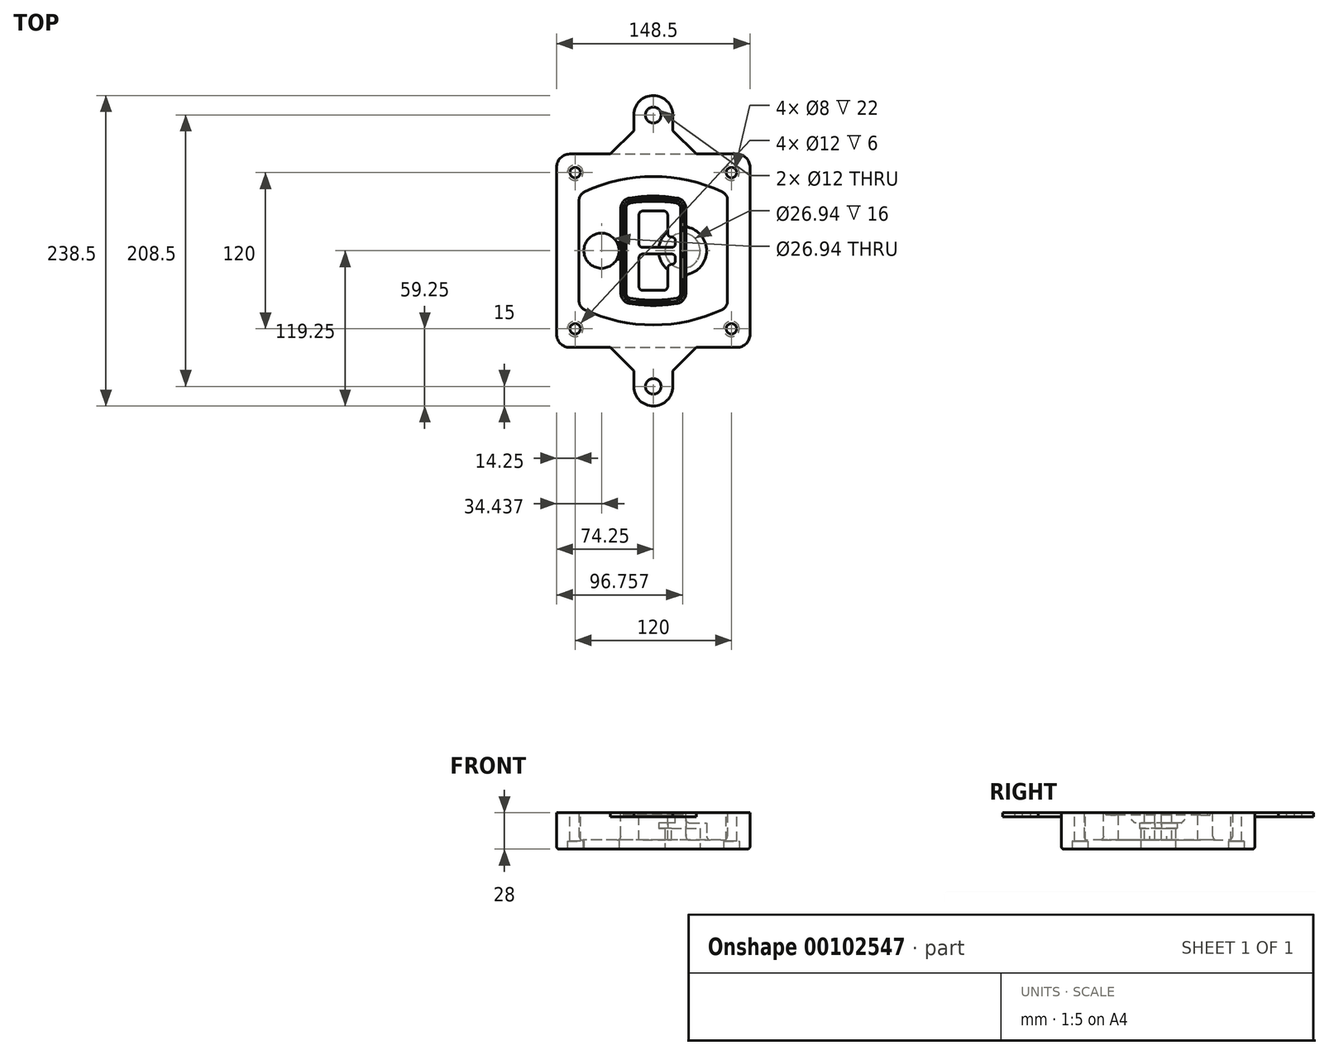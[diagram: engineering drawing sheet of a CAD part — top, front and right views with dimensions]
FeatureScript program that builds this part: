
annotation { "Feature Type Name" : "Feature", "Feature Type Description" : "" }
export const myFeature = defineFeature(function(context is Context, id is Id, definition is map)
    precondition{}
    {
        {
            var Q0;
            Q0=qCreatedBy(makeId("Top.planeOp"),FACE);
            var sketch = newSketch(context, id + "F0", { "sketchPlane" : qUnion([Q0])});
            skPoint(sketch, "E0.rect.middle", {"position": v(0, 0) * mm});
            skLineSegment(sketch, "E1.bottom", {"start": v(-64.25, -74.25) * mm, "end": v(64.25, -74.25) * mm});
            skLineSegment(sketch, "E1.top", {"start": v(-64.25, 74.25) * mm, "end": v(64.25, 74.25) * mm});
            skLineSegment(sketch, "E1.left", {"start": v(-74.25, -64.25) * mm, "end": v(-74.25, 64.25) * mm});
            skLineSegment(sketch, "E1.right", {"start": v(74.25, -64.25) * mm, "end": v(74.25, 64.25) * mm});
            skLineSegment(sketch, "E2", {"start": v(-74.25, 74.25) * mm, "end": v(74.25, -74.25) * mm, "construction": true});
            skLineSegment(sketch, "E3", {"start": v(74.25, 74.25) * mm, "end": v(-74.25, -74.25) * mm, "construction": true});
            skCircle(sketch, "E4", {"center": v(-60, 60) * mm, "radius": 4 * mm});
            skCircle(sketch, "E5", {"center": v(60, 60) * mm, "radius": 4 * mm});
            skCircle(sketch, "E6", {"center": v(60, -60) * mm, "radius": 4 * mm});
            skCircle(sketch, "E7", {"center": v(-60, -60) * mm, "radius": 4 * mm});
            skLineSegment(sketch, "E8", {"start": v(-60, 60) * mm, "end": v(60, 60) * mm, "construction": true});
            skLineSegment(sketch, "E9", {"start": v(60, 60) * mm, "end": v(60, -60) * mm, "construction": true});
            skLineSegment(sketch, "E10", {"start": v(60, -60) * mm, "end": v(-60, -60) * mm, "construction": true});
            skLineSegment(sketch, "E11", {"start": v(-60, -60) * mm, "end": v(-60, 60) * mm, "construction": true});
            skLineSegment(sketch, "E12", {"start": v(-60, 38.83) * mm, "end": v(-60, -38.83) * mm});
            skLineSegment(sketch, "E13", {"start": v(60, 38.83) * mm, "end": v(60, -38.83) * mm});
            skArc(sketch, "E14", {"start": v(54.26, 47.88) * mm, "mid": v(0, 60) * mm, "end": v(-54.26, 47.88) * mm});
            skArc(sketch, "E15", {"start": v(-54.26, -47.88) * mm, "mid": v(0, -60) * mm, "end": v(54.26, -47.88) * mm});
            skLineSegment(sketch, "E16", {"start": v(-60, 0) * mm, "end": v(60, 0) * mm, "construction": true});
            skPoint(sketch, "E17.visualSharp", {"position": v(-60, -45) * mm});
            skArc(sketch, "E17.filletArc", {"start": v(-60, -38.83) * mm, "mid": v(-58.44, -44.2) * mm, "end": v(-54.26, -47.88) * mm});
            skPoint(sketch, "E18.visualSharp", {"position": v(-60, 45) * mm});
            skArc(sketch, "E18.filletArc", {"start": v(-54.26, 47.88) * mm, "mid": v(-58.44, 44.2) * mm, "end": v(-60, 38.83) * mm});
            skPoint(sketch, "E19.visualSharp", {"position": v(60, 45) * mm});
            skArc(sketch, "E19.filletArc", {"start": v(60, 38.83) * mm, "mid": v(58.44, 44.2) * mm, "end": v(54.26, 47.88) * mm});
            skPoint(sketch, "E20.visualSharp", {"position": v(60, -45) * mm});
            skArc(sketch, "E20.filletArc", {"start": v(54.26, -47.88) * mm, "mid": v(58.44, -44.2) * mm, "end": v(60, -38.83) * mm});
            skPoint(sketch, "E21.visualSharp", {"position": v(-74.25, 74.25) * mm});
            skArc(sketch, "E21.filletArc", {"start": v(-64.25, 74.25) * mm, "mid": v(-71.32, 71.32) * mm, "end": v(-74.25, 64.25) * mm});
            skPoint(sketch, "E22.visualSharp", {"position": v(74.25, 74.25) * mm});
            skArc(sketch, "E22.filletArc", {"start": v(74.25, 64.25) * mm, "mid": v(71.32, 71.32) * mm, "end": v(64.25, 74.25) * mm});
            skPoint(sketch, "E23.visualSharp", {"position": v(74.25, -74.25) * mm});
            skArc(sketch, "E23.filletArc", {"start": v(64.25, -74.25) * mm, "mid": v(71.32, -71.32) * mm, "end": v(74.25, -64.25) * mm});
            skPoint(sketch, "E24.visualSharp", {"position": v(-74.25, -74.25) * mm});
            skArc(sketch, "E24.filletArc", {"start": v(-74.25, -64.25) * mm, "mid": v(-71.32, -71.32) * mm, "end": v(-64.25, -74.25) * mm});
            skArc(sketch, "E25.0", {"start": v(57, 38.83) * mm, "mid": v(55.9, 42.58) * mm, "end": v(52.98, 45.17) * mm});
            skLineSegment(sketch, "E25.1", {"start": v(57, 38.83) * mm, "end": v(57, -38.83) * mm});
            skArc(sketch, "E25.2", {"start": v(52.98, -45.17) * mm, "mid": v(55.9, -42.58) * mm, "end": v(57, -38.83) * mm});
            skArc(sketch, "E25.3", {"start": v(-52.98, -45.17) * mm, "mid": v(0, -57) * mm, "end": v(52.98, -45.17) * mm});
            skArc(sketch, "E25.4", {"start": v(-57, -38.83) * mm, "mid": v(-55.9, -42.58) * mm, "end": v(-52.98, -45.17) * mm});
            skArc(sketch, "E25.5", {"start": v(52.98, 45.17) * mm, "mid": v(0, 57) * mm, "end": v(-52.98, 45.17) * mm});
            skLineSegment(sketch, "E25.6", {"start": v(-57, 38.83) * mm, "end": v(-57, -38.83) * mm});
            skArc(sketch, "E25.7", {"start": v(-52.98, 45.17) * mm, "mid": v(-55.9, 42.58) * mm, "end": v(-57, 38.83) * mm});
            skArc(sketch, "E26.0", {"start": v(-55.96, 51.5) * mm, "mid": v(-61.82, 46.33) * mm, "end": v(-64, 38.83) * mm});
            skArc(sketch, "E26.1", {"start": v(55.96, 51.5) * mm, "mid": v(0, 64) * mm, "end": v(-55.96, 51.5) * mm});
            skArc(sketch, "E26.2", {"start": v(64, 38.83) * mm, "mid": v(61.82, 46.33) * mm, "end": v(55.96, 51.5) * mm});
            skLineSegment(sketch, "E26.3", {"start": v(64, 38.83) * mm, "end": v(64, -38.83) * mm});
            skArc(sketch, "E26.4", {"start": v(55.96, -51.5) * mm, "mid": v(61.82, -46.33) * mm, "end": v(64, -38.83) * mm});
            skLineSegment(sketch, "E26.5", {"start": v(-64, 38.83) * mm, "end": v(-64, -38.83) * mm});
            skArc(sketch, "E26.6", {"start": v(-55.96, -51.5) * mm, "mid": v(0, -64) * mm, "end": v(55.96, -51.5) * mm});
            skArc(sketch, "E26.7", {"start": v(-64, -38.83) * mm, "mid": v(-61.82, -46.33) * mm, "end": v(-55.96, -51.5) * mm});
            skSolve(sketch);
        }
        {
            var Q0;
            Q0=makeQuery(id+"F0.imprint","IMPRINT",FACE,{"disambiguationData":[TD([[makeQuery(id+"F0.imprint","IMPRINT",EDGE,{"derivedFrom":sQuery(id+"F0.wireOp",EDGE,"E1.bottom")}),1.0]])]});
            var Q1;
            Q1=makeQuery(id+"F0.imprint","IMPRINT",FACE,{"disambiguationData":[TD([[makeQuery(id+"F0.imprint","IMPRINT",EDGE,{"derivedFrom":sQuery(id+"F0.wireOp",EDGE,"E12")}),1.0]])]});
            var Q2;
            Q2=makeQuery(id+"F0.imprint","IMPRINT",FACE,{"disambiguationData":[TD([[makeQuery(id+"F0.imprint","IMPRINT",EDGE,{"derivedFrom":sQuery(id+"F0.wireOp",EDGE,"E25.0")}),1.0]])]});
            var Q3;
            Q3=makeQuery(id+"F0.imprint","IMPRINT",FACE,{"disambiguationData":[TD([[makeQuery(id+"F0.imprint","IMPRINT",EDGE,{"derivedFrom":sQuery(id+"F0.wireOp",EDGE,"E12")}),-1.0]])]});
            extrude(context, id + "F1", {"entities" : qUnion([Q0, Q1, Q2, Q3]), "oppositeDirection" : true, "depth" : 25 * mm});
        }
        {
            var Q0;
            Q0=makeQuery(id+"F0.imprint","IMPRINT",FACE,{"disambiguationData":[TD([[makeQuery(id+"F0.imprint","IMPRINT",EDGE,{"derivedFrom":sQuery(id+"F0.wireOp",EDGE,"E12")}),1.0]])]});
            extrude(context, id + "F2", {"entities" : qUnion([Q0]), "operationType" : NewBodyOperationType.ADD, "depth" : 3 * mm});
        }
        {
            var Q0;
            Q0=makeQuery(id+"F0.imprint","IMPRINT",FACE,{"disambiguationData":[TD([[makeQuery(id+"F0.imprint","IMPRINT",EDGE,{"derivedFrom":sQuery(id+"F0.wireOp",EDGE,"E25.0")}),1.0]])]});
            extrude(context, id + "F3", {"entities" : qUnion([Q0]), "operationType" : NewBodyOperationType.REMOVE, "oppositeDirection" : true, "depth" : 18 * mm});
        }
        {
            var Q0;
            Q0=makeQuery(id+"F2.opExtrude","CAP_FACE",FACE,{"disambiguationData":[OSD([sQuery(id+"F0.wireOp",EDGE,"E12"),sQuery(id+"F0.wireOp",EDGE,"E13"),sQuery(id+"F0.wireOp",EDGE,"E14"),sQuery(id+"F0.wireOp",EDGE,"E15"),sQuery(id+"F0.wireOp",EDGE,"E17.filletArc"),sQuery(id+"F0.wireOp",EDGE,"E18.filletArc"),sQuery(id+"F0.wireOp",EDGE,"E19.filletArc"),sQuery(id+"F0.wireOp",EDGE,"E20.filletArc"),sQuery(id+"F0.wireOp",EDGE,"E25.0"),sQuery(id+"F0.wireOp",EDGE,"E25.1"),sQuery(id+"F0.wireOp",EDGE,"E25.2"),sQuery(id+"F0.wireOp",EDGE,"E25.3"),sQuery(id+"F0.wireOp",EDGE,"E25.4"),sQuery(id+"F0.wireOp",EDGE,"E25.5"),sQuery(id+"F0.wireOp",EDGE,"E25.6"),sQuery(id+"F0.wireOp",EDGE,"E25.7")])],"isStart":false});
            var sketch = newSketch(context, id + "F4", { "sketchPlane" : qUnion([Q0])});
            skArc(sketch, "E27.0", {"start": v(-18.34, -40.45) * mm, "mid": v(0, -42) * mm, "end": v(18.34, -40.45) * mm});
            skArc(sketch, "E28.0", {"start": v(18.34, 40.45) * mm, "mid": v(0, 42) * mm, "end": v(-18.34, 40.45) * mm});
            skLineSegment(sketch, "E29", {"start": v(-25, 32.57) * mm, "end": v(-25, -32.57) * mm});
            skLineSegment(sketch, "E30", {"start": v(25, 32.57) * mm, "end": v(25, -32.57) * mm});
            skLineSegment(sketch, "E31", {"start": v(-25, 39.1) * mm, "end": v(25, 39.1) * mm, "construction": true});
            skLineSegment(sketch, "E32", {"start": v(-25, -39.1) * mm, "end": v(25, -39.1) * mm, "construction": true});
            skPoint(sketch, "E33.visualSharp", {"position": v(-25, 39.1) * mm});
            skArc(sketch, "E33.filletArc", {"start": v(-18.34, 40.45) * mm, "mid": v(-23.11, 37.73) * mm, "end": v(-25, 32.57) * mm});
            skPoint(sketch, "E34.visualSharp", {"position": v(25, 39.1) * mm});
            skArc(sketch, "E34.filletArc", {"start": v(25, 32.57) * mm, "mid": v(23.11, 37.73) * mm, "end": v(18.34, 40.45) * mm});
            skPoint(sketch, "E35.visualSharp", {"position": v(25, -39.1) * mm});
            skArc(sketch, "E35.filletArc", {"start": v(18.34, -40.45) * mm, "mid": v(23.11, -37.73) * mm, "end": v(25, -32.57) * mm});
            skPoint(sketch, "E36.visualSharp", {"position": v(-25, -39.1) * mm});
            skArc(sketch, "E36.filletArc", {"start": v(-25, -32.57) * mm, "mid": v(-23.11, -37.73) * mm, "end": v(-18.34, -40.45) * mm});
            skArc(sketch, "E37.0", {"start": v(52.98, 45.17) * mm, "mid": v(0, 57) * mm, "end": v(-52.98, 45.17) * mm});
            skArc(sketch, "E37.1", {"start": v(-52.98, 45.17) * mm, "mid": v(-55.9, 42.58) * mm, "end": v(-57, 38.83) * mm});
            skLineSegment(sketch, "E37.2", {"start": v(-57, 38.83) * mm, "end": v(-57, -38.83) * mm});
            skArc(sketch, "E37.3", {"start": v(-57, -38.83) * mm, "mid": v(-55.9, -42.58) * mm, "end": v(-52.98, -45.17) * mm});
            skArc(sketch, "E37.4", {"start": v(-52.98, -45.17) * mm, "mid": v(0, -57) * mm, "end": v(52.98, -45.17) * mm});
            skArc(sketch, "E37.5", {"start": v(52.98, -45.17) * mm, "mid": v(55.9, -42.58) * mm, "end": v(57, -38.83) * mm});
            skLineSegment(sketch, "E37.6", {"start": v(57, 38.83) * mm, "end": v(57, -38.83) * mm});
            skArc(sketch, "E37.7", {"start": v(57, 38.83) * mm, "mid": v(55.9, 42.58) * mm, "end": v(52.98, 45.17) * mm});
            skLineSegment(sketch, "E38.0", {"start": v(23, 32.57) * mm, "end": v(23, -32.57) * mm});
            skArc(sketch, "E38.1", {"start": v(18, -38.48) * mm, "mid": v(21.58, -36.44) * mm, "end": v(23, -32.57) * mm});
            skArc(sketch, "E38.2", {"start": v(-18, -38.48) * mm, "mid": v(0, -40) * mm, "end": v(18, -38.48) * mm});
            skArc(sketch, "E38.3", {"start": v(-23, -32.57) * mm, "mid": v(-21.58, -36.44) * mm, "end": v(-18, -38.48) * mm});
            skLineSegment(sketch, "E38.4", {"start": v(-23, 32.57) * mm, "end": v(-23, -32.57) * mm});
            skArc(sketch, "E38.5", {"start": v(23, 32.57) * mm, "mid": v(21.58, 36.44) * mm, "end": v(18, 38.48) * mm});
            skArc(sketch, "E38.6", {"start": v(-18, 38.48) * mm, "mid": v(-21.58, 36.44) * mm, "end": v(-23, 32.57) * mm});
            skArc(sketch, "E38.7", {"start": v(18, 38.48) * mm, "mid": v(0, 40) * mm, "end": v(-18, 38.48) * mm});
            skArc(sketch, "E39.0", {"start": v(21, 32.57) * mm, "mid": v(20.06, 35.15) * mm, "end": v(17.67, 36.5) * mm});
            skLineSegment(sketch, "E39.1", {"start": v(21, 32.57) * mm, "end": v(21, -32.57) * mm});
            skArc(sketch, "E39.2", {"start": v(17.67, -36.5) * mm, "mid": v(20.06, -35.15) * mm, "end": v(21, -32.57) * mm});
            skArc(sketch, "E39.3", {"start": v(-17.67, -36.5) * mm, "mid": v(0, -38) * mm, "end": v(17.67, -36.5) * mm});
            skArc(sketch, "E39.4", {"start": v(-21, -32.57) * mm, "mid": v(-20.06, -35.15) * mm, "end": v(-17.67, -36.5) * mm});
            skArc(sketch, "E39.5", {"start": v(17.67, 36.5) * mm, "mid": v(0, 38) * mm, "end": v(-17.67, 36.5) * mm});
            skLineSegment(sketch, "E39.6", {"start": v(-21, 32.57) * mm, "end": v(-21, -32.57) * mm});
            skArc(sketch, "E39.7", {"start": v(-17.67, 36.5) * mm, "mid": v(-20.06, 35.15) * mm, "end": v(-21, 32.57) * mm});
            skLineSegment(sketch, "E40", {"start": v(-25, 0) * mm, "end": v(25, 0) * mm, "construction": true});
            skLineSegment(sketch, "E41", {"start": v(-11, 5.5) * mm, "end": v(-11, 27.5) * mm});
            skLineSegment(sketch, "E42", {"start": v(-8, 30.5) * mm, "end": v(8, 30.5) * mm});
            skLineSegment(sketch, "E43", {"start": v(11, 27.5) * mm, "end": v(11, 13.5) * mm});
            skLineSegment(sketch, "E44", {"start": v(14, 10.5) * mm, "end": v(14, 10.5) * mm});
            skLineSegment(sketch, "E45", {"start": v(17, 7.5) * mm, "end": v(17, 5.5) * mm});
            skLineSegment(sketch, "E46", {"start": v(14, 2.5) * mm, "end": v(-8, 2.5) * mm});
            skPoint(sketch, "E47.visualSharp", {"position": v(-11, 30.5) * mm});
            skArc(sketch, "E47.filletArc", {"start": v(-8, 30.5) * mm, "mid": v(-10.12, 29.62) * mm, "end": v(-11, 27.5) * mm});
            skPoint(sketch, "E48.visualSharp", {"position": v(11, 30.5) * mm});
            skArc(sketch, "E48.filletArc", {"start": v(11, 27.5) * mm, "mid": v(10.12, 29.62) * mm, "end": v(8, 30.5) * mm});
            skPoint(sketch, "E49.visualSharp", {"position": v(11, 10.5) * mm});
            skArc(sketch, "E49.filletArc", {"start": v(11, 13.5) * mm, "mid": v(11.88, 11.38) * mm, "end": v(14, 10.5) * mm});
            skPoint(sketch, "E50.visualSharp", {"position": v(17, 10.5) * mm});
            skArc(sketch, "E50.filletArc", {"start": v(17, 7.5) * mm, "mid": v(16.12, 9.62) * mm, "end": v(14, 10.5) * mm});
            skPoint(sketch, "E51.visualSharp", {"position": v(17, 2.5) * mm});
            skArc(sketch, "E51.filletArc", {"start": v(14, 2.5) * mm, "mid": v(16.12, 3.38) * mm, "end": v(17, 5.5) * mm});
            skPoint(sketch, "E52.visualSharp", {"position": v(-11, 2.5) * mm});
            skArc(sketch, "E52.filletArc", {"start": v(-11, 5.5) * mm, "mid": v(-10.12, 3.38) * mm, "end": v(-8, 2.5) * mm});
            skLineSegment(sketch, "E53.0.MirrorCS", {"start": v(14, -2.5) * mm, "end": v(-8, -2.5) * mm});
            skArc(sketch, "E54.0.MirrorCS", {"start": v(-11, -5.5) * mm, "mid": v(-10.12, -3.38) * mm, "end": v(-8, -2.5) * mm});
            skLineSegment(sketch, "E55.0.MirrorCS", {"start": v(-11, -5.5) * mm, "end": v(-11, -27.5) * mm});
            skArc(sketch, "E56.0.MirrorCS", {"start": v(-8, -30.5) * mm, "mid": v(-10.12, -29.62) * mm, "end": v(-11, -27.5) * mm});
            skLineSegment(sketch, "E57.0.MirrorCS", {"start": v(-8, -30.5) * mm, "end": v(8, -30.5) * mm});
            skArc(sketch, "E58.0.MirrorCS", {"start": v(11, -27.5) * mm, "mid": v(10.12, -29.62) * mm, "end": v(8, -30.5) * mm});
            skLineSegment(sketch, "E59.0.MirrorCS", {"start": v(11, -27.5) * mm, "end": v(11, -13.5) * mm});
            skArc(sketch, "E60.0.MirrorCS", {"start": v(11, -13.5) * mm, "mid": v(11.88, -11.38) * mm, "end": v(14, -10.5) * mm});
            skArc(sketch, "E61.0.MirrorCS", {"start": v(17, -7.5) * mm, "mid": v(16.12, -9.62) * mm, "end": v(14, -10.5) * mm});
            skLineSegment(sketch, "E62.0.MirrorCS", {"start": v(17, -7.5) * mm, "end": v(17, -5.5) * mm});
            skArc(sketch, "E63.0.MirrorCS", {"start": v(14, -2.5) * mm, "mid": v(16.12, -3.38) * mm, "end": v(17, -5.5) * mm});
            skSolve(sketch);
        }
        {
            var Q0;
            Q0=makeQuery(id+"F4.imprint","IMPRINT",FACE,{"disambiguationData":[TD([[makeQuery(id+"F4.imprint","IMPRINT",EDGE,{"derivedFrom":sQuery(id+"F4.wireOp",EDGE,"E27.0")}),1.0]])]});
            var Q1;
            Q1=makeQuery(id+"F4.imprint","IMPRINT",FACE,{"disambiguationData":[TD([[makeQuery(id+"F4.imprint","IMPRINT",EDGE,{"derivedFrom":sQuery(id+"F4.wireOp",EDGE,"E38.0")}),-1.0]])]});
            var Q2;
            Q2=makeQuery(id+"F4.imprint","IMPRINT",FACE,{"disambiguationData":[TD([[makeQuery(id+"F4.imprint","IMPRINT",EDGE,{"derivedFrom":sQuery(id+"F4.wireOp",EDGE,"E39.0")}),1.0]])]});
            extrude(context, id + "F5", {"entities" : qUnion([Q0, Q1, Q2]), "operationType" : NewBodyOperationType.ADD, "endBound" : BoundingType.UP_TO_NEXT, "oppositeDirection" : true, "depth" : 25 * mm});
        }
        {
            var Q0;
            Q0=makeQuery(id+"F4.imprint","IMPRINT",FACE,{"disambiguationData":[TD([[makeQuery(id+"F4.imprint","IMPRINT",EDGE,{"derivedFrom":sQuery(id+"F4.wireOp",EDGE,"E38.0")}),-1.0]])]});
            extrude(context, id + "F6", {"entities" : qUnion([Q0]), "operationType" : NewBodyOperationType.REMOVE, "oppositeDirection" : true, "depth" : 2 * mm});
        }
        {
            var Q0;
            Q0=makeQuery(id+"F1.opExtrude","CAP_FACE",FACE,{"disambiguationData":[OSD([sQuery(id+"F0.wireOp",EDGE,"E1.bottom"),sQuery(id+"F0.wireOp",EDGE,"E1.top"),sQuery(id+"F0.wireOp",EDGE,"E1.left"),sQuery(id+"F0.wireOp",EDGE,"E1.right"),sQuery(id+"F0.wireOp",EDGE,"E4"),sQuery(id+"F0.wireOp",EDGE,"E5"),sQuery(id+"F0.wireOp",EDGE,"E6"),sQuery(id+"F0.wireOp",EDGE,"E7"),sQuery(id+"F0.wireOp",EDGE,"E21.filletArc"),sQuery(id+"F0.wireOp",EDGE,"E22.filletArc"),sQuery(id+"F0.wireOp",EDGE,"E23.filletArc"),sQuery(id+"F0.wireOp",EDGE,"E24.filletArc")])],"isStart":false});
            var sketch = newSketch(context, id + "F7", { "sketchPlane" : qUnion([Q0])});
            skCircle(sketch, "E64", {"center": v(22.5, 0) * mm, "radius": 13.47 * mm});
            skCircle(sketch, "E65", {"center": v(-39.81, 0) * mm, "radius": 13.47 * mm});
            skLineSegment(sketch, "E66", {"start": v(74.25, 0) * mm, "end": v(-74.25, 0) * mm});
            skCircle(sketch, "E67", {"center": v(22.5, 0) * mm, "radius": 18.47 * mm});
            skCircle(sketch, "E68", {"center": v(60, -60) * mm, "radius": 6 * mm});
            skCircle(sketch, "E69", {"center": v(-60, -60) * mm, "radius": 6 * mm});
            skCircle(sketch, "E70", {"center": v(-60, 60) * mm, "radius": 6 * mm});
            skCircle(sketch, "E71", {"center": v(60, 60) * mm, "radius": 6 * mm});
            skSolve(sketch);
        }
        {
            var Q0;
            {var subQ1=sQuery(id+"F7.wireOp",EDGE,"E66");var subQ4=sQuery(id+"F7.wireOp",EDGE,"E64");var subQ6=makeQuery(id+"F7.imprint","INTERSECT",VERTEX,{"disambiguationData":[OD(0.0)],"derivedFrom":[subQ4,subQ1]});Q0=makeQuery(id+"F7.imprint","IMPRINT",FACE,{"disambiguationData":[TD([[makeQuery(id+"F7.imprint","IMPRINT",EDGE,{"disambiguationData":[TD([[subQ6,-1.0]])],"derivedFrom":subQ4}),-1.0]])]});}
            var Q1;
            {var subQ0=sQuery(id+"F7.wireOp",EDGE,"E66");var subQ1=sQuery(id+"F7.wireOp",EDGE,"E64");var subQ3=makeQuery(id+"F7.imprint","INTERSECT",VERTEX,{"disambiguationData":[OD(0.0)],"derivedFrom":[subQ1,subQ0]});Q1=makeQuery(id+"F7.imprint","IMPRINT",FACE,{"disambiguationData":[TD([[makeQuery(id+"F7.imprint","IMPRINT",EDGE,{"disambiguationData":[TD([[subQ3,-1.0]])],"derivedFrom":subQ1}),1.0]])]});}
            var Q2;
            {var subQ0=sQuery(id+"F7.wireOp",EDGE,"E66");var subQ1=sQuery(id+"F7.wireOp",EDGE,"E64");var subQ3=makeQuery(id+"F7.imprint","INTERSECT",VERTEX,{"disambiguationData":[OD(0.0)],"derivedFrom":[subQ1,subQ0]});Q2=makeQuery(id+"F7.imprint","IMPRINT",FACE,{"disambiguationData":[TD([[makeQuery(id+"F7.imprint","IMPRINT",EDGE,{"disambiguationData":[TD([[subQ3,1.0]])],"derivedFrom":subQ1}),1.0]])]});}
            var Q3;
            {var subQ1=sQuery(id+"F7.wireOp",EDGE,"E66");var subQ4=sQuery(id+"F7.wireOp",EDGE,"E64");var subQ6=makeQuery(id+"F7.imprint","INTERSECT",VERTEX,{"disambiguationData":[OD(0.0)],"derivedFrom":[subQ4,subQ1]});Q3=makeQuery(id+"F7.imprint","IMPRINT",FACE,{"disambiguationData":[TD([[makeQuery(id+"F7.imprint","IMPRINT",EDGE,{"disambiguationData":[TD([[subQ6,1.0]])],"derivedFrom":subQ4}),-1.0]])]});}
            extrude(context, id + "F8", {"entities" : qUnion([Q0, Q1, Q2, Q3]), "operationType" : NewBodyOperationType.ADD, "oppositeDirection" : true, "depth" : 20 * mm});
        }
        {
            var Q0;
            {var subQ0=sQuery(id+"F7.wireOp",EDGE,"E66");var subQ1=sQuery(id+"F7.wireOp",EDGE,"E64");var subQ3=makeQuery(id+"F7.imprint","INTERSECT",VERTEX,{"disambiguationData":[OD(0.0)],"derivedFrom":[subQ1,subQ0]});Q0=makeQuery(id+"F7.imprint","IMPRINT",FACE,{"disambiguationData":[TD([[makeQuery(id+"F7.imprint","IMPRINT",EDGE,{"disambiguationData":[TD([[subQ3,-1.0]])],"derivedFrom":subQ1}),1.0]])]});}
            var Q1;
            {var subQ0=sQuery(id+"F7.wireOp",EDGE,"E66");var subQ1=sQuery(id+"F7.wireOp",EDGE,"E64");var subQ3=makeQuery(id+"F7.imprint","INTERSECT",VERTEX,{"disambiguationData":[OD(0.0)],"derivedFrom":[subQ1,subQ0]});Q1=makeQuery(id+"F7.imprint","IMPRINT",FACE,{"disambiguationData":[TD([[makeQuery(id+"F7.imprint","IMPRINT",EDGE,{"disambiguationData":[TD([[subQ3,1.0]])],"derivedFrom":subQ1}),1.0]])]});}
            extrude(context, id + "F9", {"entities" : qUnion([Q0, Q1]), "operationType" : NewBodyOperationType.REMOVE, "oppositeDirection" : true, "depth" : 16 * mm});
        }
        {
            var Q0;
            {var subQ0=sQuery(id+"F7.wireOp",EDGE,"E66");var subQ1=sQuery(id+"F7.wireOp",EDGE,"E65");var subQ3=makeQuery(id+"F7.imprint","INTERSECT",VERTEX,{"disambiguationData":[OD(0.0)],"derivedFrom":[subQ1,subQ0]});Q0=makeQuery(id+"F7.imprint","IMPRINT",FACE,{"disambiguationData":[TD([[makeQuery(id+"F7.imprint","IMPRINT",EDGE,{"disambiguationData":[TD([[subQ3,-1.0]])],"derivedFrom":subQ1}),1.0]])]});}
            var Q1;
            {var subQ0=sQuery(id+"F7.wireOp",EDGE,"E66");var subQ1=sQuery(id+"F7.wireOp",EDGE,"E65");var subQ3=makeQuery(id+"F7.imprint","INTERSECT",VERTEX,{"disambiguationData":[OD(0.0)],"derivedFrom":[subQ1,subQ0]});Q1=makeQuery(id+"F7.imprint","IMPRINT",FACE,{"disambiguationData":[TD([[makeQuery(id+"F7.imprint","IMPRINT",EDGE,{"disambiguationData":[TD([[subQ3,1.0]])],"derivedFrom":subQ1}),1.0]])]});}
            extrude(context, id + "F10", {"entities" : qUnion([Q0, Q1]), "operationType" : NewBodyOperationType.REMOVE, "oppositeDirection" : true, "depth" : 25 * mm});
        }
        {
            var Q0;
            Q0=makeQuery(id+"F7.imprint","IMPRINT",FACE,{"disambiguationData":[TD([[makeQuery(id+"F7.imprint","IMPRINT",EDGE,{"derivedFrom":sQuery(id+"F7.wireOp",EDGE,"E68")}),1.0]])]});
            var Q1;
            Q1=makeQuery(id+"F7.imprint","IMPRINT",FACE,{"disambiguationData":[TD([[makeQuery(id+"F7.imprint","IMPRINT",EDGE,{"derivedFrom":makeQuery(id+"F1.opExtrude","CAP_EDGE",EDGE,{"disambiguationData":[OSD([sQuery(id+"F0.wireOp",EDGE,"E5")])],"isStart":false})}),-1.0]])]});
            var Q2;
            Q2=makeQuery(id+"F7.imprint","IMPRINT",FACE,{"disambiguationData":[TD([[makeQuery(id+"F7.imprint","IMPRINT",EDGE,{"derivedFrom":sQuery(id+"F7.wireOp",EDGE,"E69")}),1.0]])]});
            var Q3;
            Q3=makeQuery(id+"F7.imprint","IMPRINT",FACE,{"disambiguationData":[TD([[makeQuery(id+"F7.imprint","IMPRINT",EDGE,{"derivedFrom":makeQuery(id+"F1.opExtrude","CAP_EDGE",EDGE,{"disambiguationData":[OSD([sQuery(id+"F0.wireOp",EDGE,"E4")])],"isStart":false})}),-1.0]])]});
            var Q4;
            Q4=makeQuery(id+"F7.imprint","IMPRINT",FACE,{"disambiguationData":[TD([[makeQuery(id+"F7.imprint","IMPRINT",EDGE,{"derivedFrom":sQuery(id+"F7.wireOp",EDGE,"E70")}),1.0]])]});
            var Q5;
            Q5=makeQuery(id+"F7.imprint","IMPRINT",FACE,{"disambiguationData":[TD([[makeQuery(id+"F7.imprint","IMPRINT",EDGE,{"derivedFrom":makeQuery(id+"F1.opExtrude","CAP_EDGE",EDGE,{"disambiguationData":[OSD([sQuery(id+"F0.wireOp",EDGE,"E7")])],"isStart":false})}),-1.0]])]});
            var Q6;
            Q6=makeQuery(id+"F7.imprint","IMPRINT",FACE,{"disambiguationData":[TD([[makeQuery(id+"F7.imprint","IMPRINT",EDGE,{"derivedFrom":sQuery(id+"F7.wireOp",EDGE,"E71")}),1.0]])]});
            var Q7;
            Q7=makeQuery(id+"F7.imprint","IMPRINT",FACE,{"disambiguationData":[TD([[makeQuery(id+"F7.imprint","IMPRINT",EDGE,{"derivedFrom":makeQuery(id+"F1.opExtrude","CAP_EDGE",EDGE,{"disambiguationData":[OSD([sQuery(id+"F0.wireOp",EDGE,"E6")])],"isStart":false})}),-1.0]])]});
            extrude(context, id + "F11", {"entities" : qUnion([Q0, Q1, Q2, Q3, Q4, Q5, Q6, Q7]), "operationType" : NewBodyOperationType.REMOVE, "oppositeDirection" : true, "depth" : 6 * mm});
        }
        {
            var Q0;
            Q0=makeQuery(id+"F9.boolean.opBoolean","COPY",FACE,{"derivedFrom":makeQuery(id+"F9.opExtrude","CAP_FACE",FACE,{"disambiguationData":[OSD([sQuery(id+"F7.wireOp",EDGE,"E64")])],"isStart":false})});
            var sketch = newSketch(context, id + "F12", { "sketchPlane" : qUnion([Q0])});
            skArc(sketch, "E72.0", {"start": v(11, 14.45) * mm, "mid": v(6.45, 9.13) * mm, "end": v(4.2, 2.5) * mm});
            skArc(sketch, "E72.1", {"start": v(4.2, -2.5) * mm, "mid": v(6.45, -9.13) * mm, "end": v(11, -14.45) * mm});
            skLineSegment(sketch, "E73", {"start": v(4.2, -2.5) * mm, "end": v(14, -2.5) * mm});
            skLineSegment(sketch, "E74.0", {"start": v(14, 2.5) * mm, "end": v(4.2, 2.5) * mm});
            skArc(sketch, "E74.1", {"start": v(14, 2.5) * mm, "mid": v(16.12, 3.38) * mm, "end": v(17, 5.5) * mm});
            skLineSegment(sketch, "E74.2", {"start": v(17, 7.5) * mm, "end": v(17, 5.5) * mm});
            skArc(sketch, "E74.3", {"start": v(17, 7.5) * mm, "mid": v(16.12, 9.62) * mm, "end": v(14, 10.5) * mm});
            skArc(sketch, "E74.4", {"start": v(11, 13.5) * mm, "mid": v(11.88, 11.38) * mm, "end": v(14, 10.5) * mm});
            skLineSegment(sketch, "E74.5", {"start": v(11, 14.45) * mm, "end": v(11, 13.5) * mm});
            skLineSegment(sketch, "E74.7", {"start": v(14, -2.5) * mm, "end": v(4.2, -2.5) * mm});
            skArc(sketch, "E74.8", {"start": v(14, -2.5) * mm, "mid": v(16.12, -3.38) * mm, "end": v(17, -5.5) * mm});
            skLineSegment(sketch, "E74.9", {"start": v(17, -7.5) * mm, "end": v(17, -5.5) * mm});
            skArc(sketch, "E74.10", {"start": v(17, -7.5) * mm, "mid": v(16.12, -9.62) * mm, "end": v(14, -10.5) * mm});
            skArc(sketch, "E74.11", {"start": v(11, -13.5) * mm, "mid": v(11.88, -11.38) * mm, "end": v(14, -10.5) * mm});
            skLineSegment(sketch, "E74.12", {"start": v(11, -14.45) * mm, "end": v(11, -13.5) * mm});
            skPoint(sketch, "E75.orphan", {"position": v(11, -27.5) * mm});
            skPoint(sketch, "E76.orphan", {"position": v(-8, -2.5) * mm});
            skPoint(sketch, "E77.orphan", {"position": v(-8, 2.5) * mm});
            skPoint(sketch, "E78.orphan", {"position": v(11, 27.5) * mm});
            skSolve(sketch);
        }
        {
            var Q0;
            {var subQ7=sQuery(id+"F12.wireOp",EDGE,"E72.0");var subQ14=sQuery(id+"F12.wireOp",EDGE,"E72.1");var subQ16=sQuery(id+"F12.wireOp",EDGE,"E74.1");var subQ18=sQuery(id+"F12.wireOp",EDGE,"E74.8");Q0=qUnion([makeQuery(id+"F12.imprint","IMPRINT",FACE,{"disambiguationData":[TD([[makeQuery(id+"F12.imprint","IMPRINT",EDGE,{"derivedFrom":subQ7}),1.0]])]}),makeQuery(id+"F12.imprint","IMPRINT",FACE,{"disambiguationData":[TD([[makeQuery(id+"F12.imprint","IMPRINT",EDGE,{"derivedFrom":subQ14}),1.0]])]}),makeQuery(id+"F12.imprint","IMPRINT",FACE,{"disambiguationData":[TD([[makeQuery(id+"F12.imprint","IMPRINT",EDGE,{"derivedFrom":subQ16}),1.0]])]}),makeQuery(id+"F12.imprint","IMPRINT",FACE,{"disambiguationData":[TD([[makeQuery(id+"F12.imprint","IMPRINT",EDGE,{"derivedFrom":subQ18}),-1.0]])]})]);}
            var Q1;
            Q1=makeQuery(id+"F5.boolean.opBoolean","SPLIT",FACE,{"disambiguationData":[TD([makeQuery(id+"F5.opExtrude","SWEPT_FACE",FACE,{"disambiguationData":[OSD([sQuery(id+"F4.wireOp",EDGE,"E41")])]})])],"derivedFrom":makeQuery(id+"F3.boolean.opBoolean","COPY",FACE,{"derivedFrom":makeQuery(id+"F3.opExtrude","CAP_FACE",FACE,{"disambiguationData":[OSD([sQuery(id+"F0.wireOp",EDGE,"E25.0"),sQuery(id+"F0.wireOp",EDGE,"E25.1"),sQuery(id+"F0.wireOp",EDGE,"E25.2"),sQuery(id+"F0.wireOp",EDGE,"E25.3"),sQuery(id+"F0.wireOp",EDGE,"E25.4"),sQuery(id+"F0.wireOp",EDGE,"E25.5"),sQuery(id+"F0.wireOp",EDGE,"E25.6"),sQuery(id+"F0.wireOp",EDGE,"E25.7")])],"isStart":false})})});
            extrude(context, id + "F13", {"entities" : qUnion([Q0]), "operationType" : NewBodyOperationType.REMOVE, "endBound" : BoundingType.UP_TO_SURFACE, "endBoundEntityFace" : qUnion([Q1]), "depth" : 25 * mm});
        }
        {
            var Q0;
            Q0=makeQuery(id+"F3.boolean.opBoolean","COPY",EDGE,{"derivedFrom":makeQuery(id+"F3.opExtrude","CAP_EDGE",EDGE,{"disambiguationData":[OSD([sQuery(id+"F0.wireOp",EDGE,"E25.6")])],"isStart":false})});
            var Q1;
            Q1=makeQuery(id+"F8.boolean.opBoolean","INTERSECT",EDGE,{"derivedFrom":[makeQuery(id+"F5.opExtrude","SWEPT_FACE",FACE,{"disambiguationData":[OSD([sQuery(id+"F4.wireOp",EDGE,"E30")])]}),makeQuery(id+"F8.opExtrude","CAP_FACE",FACE,{"disambiguationData":[OSD([sQuery(id+"F7.wireOp",EDGE,"E67")])],"isStart":false})]});
            var Q2;
            Q2=makeQuery(id+"F8.boolean.opBoolean","INTERSECT",EDGE,{"disambiguationData":[OD(1.0)],"derivedFrom":[makeQuery(id+"F5.opExtrude","SWEPT_FACE",FACE,{"disambiguationData":[OSD([sQuery(id+"F4.wireOp",EDGE,"E30")])]}),makeQuery(id+"F8.opExtrude","SWEPT_FACE",FACE,{"disambiguationData":[OSD([sQuery(id+"F7.wireOp",EDGE,"E67")])]})]});
            var Q3;
            {var subQ0=sQuery(id+"F4.wireOp",EDGE,"E30");Q3=makeQuery(id+"F8.boolean.opBoolean","SPLIT",EDGE,{"disambiguationData":[TD([makeQuery(id+"F5.opExtrude","SWEPT_FACE",FACE,{"disambiguationData":[OSD([sQuery(id+"F4.wireOp",EDGE,"E35.filletArc")])]})])],"derivedFrom":makeQuery(id+"F5.opExtrude","CAP_EDGE",EDGE,{"disambiguationData":[OSD([subQ0])],"isStart":false})});}
            var Q4;
            {var subQ0=sQuery(id+"F0.wireOp",EDGE,"E25.7");var subQ1=sQuery(id+"F0.wireOp",EDGE,"E25.1");var subQ2=sQuery(id+"F0.wireOp",EDGE,"E25.6");var subQ3=sQuery(id+"F0.wireOp",EDGE,"E25.5");var subQ4=sQuery(id+"F0.wireOp",EDGE,"E25.4");var subQ5=sQuery(id+"F0.wireOp",EDGE,"E25.0");var subQ6=sQuery(id+"F0.wireOp",EDGE,"E25.2");var subQ7=sQuery(id+"F0.wireOp",EDGE,"E25.3");Q4=makeQuery(id+"F8.boolean.opBoolean","INTERSECT",EDGE,{"derivedFrom":[makeQuery(id+"F5.boolean.opBoolean","SPLIT",FACE,{"disambiguationData":[TD([makeQuery(id+"F2.opExtrude","SWEPT_FACE",FACE,{"disambiguationData":[OSD([subQ5])]})])],"derivedFrom":makeQuery(id+"F3.boolean.opBoolean","COPY",FACE,{"derivedFrom":makeQuery(id+"F3.opExtrude","CAP_FACE",FACE,{"disambiguationData":[OSD([subQ5,subQ1,subQ6,subQ7,subQ4,subQ3,subQ2,subQ0])],"isStart":false})})}),makeQuery(id+"F8.opExtrude","SWEPT_FACE",FACE,{"disambiguationData":[OSD([sQuery(id+"F7.wireOp",EDGE,"E67")])]})]});}
            var Q5;
            Q5=makeQuery(id+"F8.boolean.opBoolean","INTERSECT",EDGE,{"disambiguationData":[OD(0.0)],"derivedFrom":[makeQuery(id+"F5.opExtrude","SWEPT_FACE",FACE,{"disambiguationData":[OSD([sQuery(id+"F4.wireOp",EDGE,"E30")])]}),makeQuery(id+"F8.opExtrude","SWEPT_FACE",FACE,{"disambiguationData":[OSD([sQuery(id+"F7.wireOp",EDGE,"E67")])]})]});
            fillet(context, id + "F14", {"entities" : qUnion([Q0, Q1, Q2, Q3, Q4, Q5]), "radius" : 3 * mm, "tangentPropagation" : true, "allowEdgeOverflow" : false});
        }
        {
            var Q0;
            Q0=makeQuery(id+"F1.opExtrude","CAP_EDGE",EDGE,{"disambiguationData":[OSD([sQuery(id+"F0.wireOp",EDGE,"E1.bottom")])],"isStart":false});
            fillet(context, id + "F15", {"entities" : qUnion([Q0]), "radius" : 2 * mm, "tangentPropagation" : true, "allowEdgeOverflow" : false});
        }
        {
            var Q0;
            {var subQ0=sQuery(id+"F0.wireOp",EDGE,"E22.filletArc");var subQ1=sQuery(id+"F0.wireOp",EDGE,"E7");var subQ2=sQuery(id+"F0.wireOp",EDGE,"E6");var subQ3=sQuery(id+"F0.wireOp",EDGE,"E5");var subQ4=sQuery(id+"F0.wireOp",EDGE,"E4");var subQ5=sQuery(id+"F0.wireOp",EDGE,"E1.bottom");var subQ6=sQuery(id+"F0.wireOp",EDGE,"E21.filletArc");var subQ7=sQuery(id+"F0.wireOp",EDGE,"E1.top");var subQ8=sQuery(id+"F0.wireOp",EDGE,"E1.left");var subQ9=sQuery(id+"F0.wireOp",EDGE,"E1.right");var subQ10=sQuery(id+"F0.wireOp",EDGE,"E23.filletArc");var subQ11=sQuery(id+"F0.wireOp",EDGE,"E24.filletArc");Q0=makeQuery(id+"F2.boolean.opBoolean","SPLIT",FACE,{"disambiguationData":[TD([makeQuery(id+"F1.opExtrude","SWEPT_FACE",FACE,{"disambiguationData":[OSD([subQ5])]})])],"derivedFrom":makeQuery(id+"F1.opExtrude","CAP_FACE",FACE,{"disambiguationData":[OSD([subQ5,subQ7,subQ8,subQ9,subQ4,subQ3,subQ2,subQ1,subQ6,subQ0,subQ10,subQ11])],"isStart":true})});}
            var sketch = newSketch(context, id + "F16", { "sketchPlane" : qUnion([Q0])});
            skLineSegment(sketch, "E79", {"start": v(0, 74.25) * mm, "end": v(0, 104.25) * mm, "construction": true});
            skArc(sketch, "E80", {"start": v(15, 104.25) * mm, "mid": v(-0.14, 119.25) * mm, "end": v(-15, 103.96) * mm});
            skLineSegment(sketch, "E81", {"start": v(-33, 74.25) * mm, "end": v(-15, 92.25) * mm});
            skLineSegment(sketch, "E82", {"start": v(-15, 92.25) * mm, "end": v(-15, 104.54) * mm});
            skLineSegment(sketch, "E83", {"start": v(33, 74.25) * mm, "end": v(15, 92.25) * mm});
            skLineSegment(sketch, "E84", {"start": v(15, 92.25) * mm, "end": v(15, 104.25) * mm});
            skArc(sketch, "E85", {"start": v(15, 104.25) * mm, "mid": v(0.14, 119.25) * mm, "end": v(-15, 104.54) * mm});
            skCircle(sketch, "E86", {"center": v(0, 104.25) * mm, "radius": 6 * mm});
            skLineSegment(sketch, "E87", {"start": v(-74.25, 0) * mm, "end": v(74.25, 0) * mm, "construction": true});
            skLineSegment(sketch, "E88.MirrorCS", {"start": v(33, -74.25) * mm, "end": v(15, -92.25) * mm});
            skLineSegment(sketch, "E89.MirrorCS", {"start": v(15, -92.25) * mm, "end": v(15, -104.25) * mm});
            skArc(sketch, "E90.MirrorCS", {"start": v(15, -104.25) * mm, "mid": v(0.14, -119.25) * mm, "end": v(-15, -104.54) * mm});
            skLineSegment(sketch, "E91.MirrorCS", {"start": v(-15, -92.25) * mm, "end": v(-15, -104.54) * mm});
            skLineSegment(sketch, "E92.MirrorCS", {"start": v(-33, -74.25) * mm, "end": v(-15, -92.25) * mm});
            skLineSegment(sketch, "E93.MirrorCS", {"start": v(0, -74.25) * mm, "end": v(0, -104.25) * mm, "construction": true});
            skCircle(sketch, "E94.MirrorC", {"center": v(0, -104.25) * mm, "radius": 6 * mm});
            skSolve(sketch);
        }
        {
            var Q0;
            {var subQ0=sQuery(id+"F16.wireOp",EDGE,"E88.MirrorCS");Q0=makeQuery(id+"F16.imprint","IMPRINT",FACE,{"disambiguationData":[TD([[makeQuery(id+"F16.imprint","IMPRINT",EDGE,{"derivedFrom":subQ0}),-1.0]])]});}
            var Q1;
            Q1=makeQuery(id+"F16.imprint","IMPRINT",FACE,{"disambiguationData":[TD([[makeQuery(id+"F16.imprint","IMPRINT",EDGE,{"derivedFrom":makeQuery(id+"F1.opExtrude","CAP_EDGE",EDGE,{"disambiguationData":[OSD([sQuery(id+"F0.wireOp",EDGE,"E1.left")])],"isStart":true})}),-1.0]])]});
            var Q2;
            {var subQ4=sQuery(id+"F16.wireOp",EDGE,"E81");Q2=makeQuery(id+"F16.imprint","IMPRINT",FACE,{"disambiguationData":[TD([[makeQuery(id+"F16.imprint","IMPRINT",EDGE,{"derivedFrom":subQ4}),-1.0]])]});}
            var Q3;
            Q3=makeQuery(id+"F2.opExtrude","CAP_FACE",FACE,{"disambiguationData":[OSD([sQuery(id+"F0.wireOp",EDGE,"E12"),sQuery(id+"F0.wireOp",EDGE,"E13"),sQuery(id+"F0.wireOp",EDGE,"E14"),sQuery(id+"F0.wireOp",EDGE,"E15"),sQuery(id+"F0.wireOp",EDGE,"E17.filletArc"),sQuery(id+"F0.wireOp",EDGE,"E18.filletArc"),sQuery(id+"F0.wireOp",EDGE,"E19.filletArc"),sQuery(id+"F0.wireOp",EDGE,"E20.filletArc"),sQuery(id+"F0.wireOp",EDGE,"E25.0"),sQuery(id+"F0.wireOp",EDGE,"E25.1"),sQuery(id+"F0.wireOp",EDGE,"E25.2"),sQuery(id+"F0.wireOp",EDGE,"E25.3"),sQuery(id+"F0.wireOp",EDGE,"E25.4"),sQuery(id+"F0.wireOp",EDGE,"E25.5"),sQuery(id+"F0.wireOp",EDGE,"E25.6"),sQuery(id+"F0.wireOp",EDGE,"E25.7")])],"isStart":false});
            extrude(context, id + "F17", {"entities" : qUnion([Q0, Q1, Q2]), "operationType" : NewBodyOperationType.ADD, "endBound" : BoundingType.UP_TO_SURFACE, "endBoundEntityFace" : qUnion([Q3]), "depth" : 25 * mm});
        }
    });
